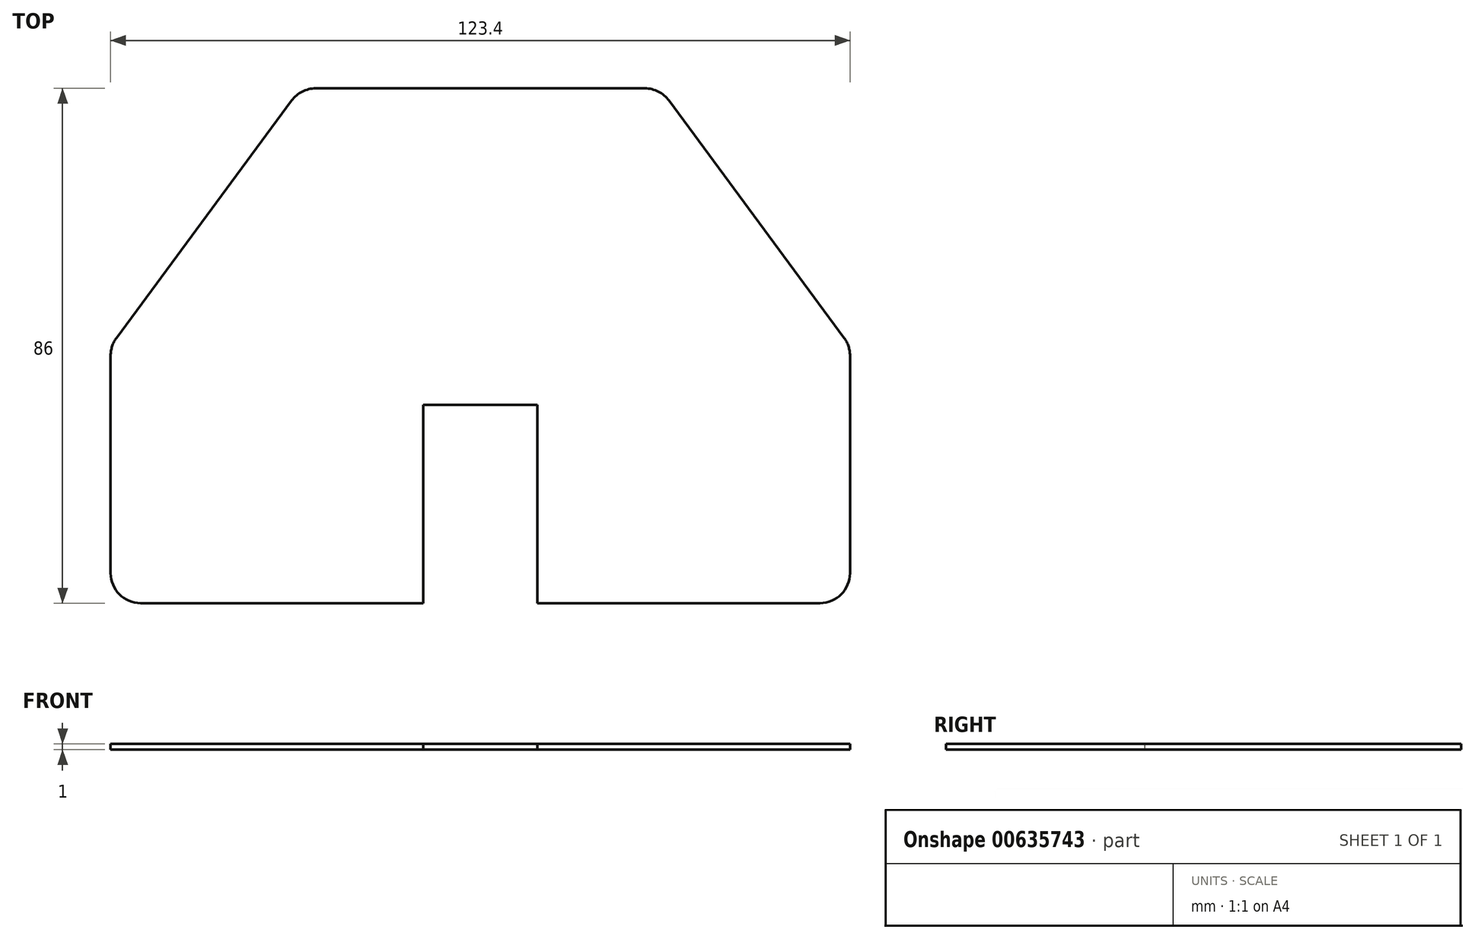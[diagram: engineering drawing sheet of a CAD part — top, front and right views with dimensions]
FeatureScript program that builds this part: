
annotation { "Feature Type Name" : "Feature", "Feature Type Description" : "" }
export const myFeature = defineFeature(function(context is Context, id is Id, definition is map)
    precondition{}
    {
        {
            var Q0;
            Q0=qCreatedBy(makeId("Top.planeOp"),FACE);
            var sketch = newSketch(context, id + "F0", { "sketchPlane" : qUnion([Q0])});
            skLineSegment(sketch, "E0.bottom", {"start": v(-61.7, 21.5) * mm, "end": v(61.7, 21.5) * mm});
            skLineSegment(sketch, "E0.top", {"start": v(-61.7, -21.5) * mm, "end": v(61.7, -21.5) * mm});
            skLineSegment(sketch, "E0.left", {"start": v(-61.7, 21.5) * mm, "end": v(-61.7, -21.5) * mm});
            skLineSegment(sketch, "E0.right", {"start": v(61.7, 21.5) * mm, "end": v(61.7, -21.5) * mm});
            skPoint(sketch, "E0.middle", {"position": v(0, 0) * mm});
            skLineSegment(sketch, "E1", {"start": v(0, 21.5) * mm, "end": v(0, 64.5) * mm});
            skPoint(sketch, "E1.endSnap0", {"position": v(0, 21.5) * mm});
            skLineSegment(sketch, "E2", {"start": v(0, 64.5) * mm, "end": v(30, 64.5) * mm});
            skLineSegment(sketch, "E3", {"start": v(0, 64.5) * mm, "end": v(-30, 64.5) * mm});
            skLineSegment(sketch, "E4", {"start": v(-30, 64.5) * mm, "end": v(-61.7, 21.5) * mm});
            skLineSegment(sketch, "E5", {"start": v(30, 64.5) * mm, "end": v(61.7, 21.5) * mm});
            skLineSegment(sketch, "E6.bottom", {"start": v(9.54, -21.5) * mm, "end": v(-9.54, -21.5) * mm});
            skLineSegment(sketch, "E6.top", {"start": v(9.54, 11.65) * mm, "end": v(-9.54, 11.65) * mm});
            skLineSegment(sketch, "E6.left", {"start": v(9.54, -21.5) * mm, "end": v(9.54, 11.65) * mm});
            skLineSegment(sketch, "E6.right", {"start": v(-9.54, -21.5) * mm, "end": v(-9.54, 11.65) * mm});
            skPoint(sketch, "E7", {"position": v(0, 11.65) * mm});
            skSolve(sketch);
        }
        {
            var Q0;
            {var subQ2=sQuery(id+"F0.wireOp",EDGE,"E1");Q0=makeQuery(id+"F0.imprint","IMPRINT",FACE,{"disambiguationData":[TD([[makeQuery(id+"F0.imprint","IMPRINT",EDGE,{"derivedFrom":subQ2}),1.0]])]});}
            var Q1;
            {var subQ2=sQuery(id+"F0.wireOp",EDGE,"E1");Q1=makeQuery(id+"F0.imprint","IMPRINT",FACE,{"disambiguationData":[TD([[makeQuery(id+"F0.imprint","IMPRINT",EDGE,{"derivedFrom":subQ2}),-1.0]])]});}
            var Q2;
            {var subQ5=sQuery(id+"F0.wireOp",EDGE,"E0.left");Q2=makeQuery(id+"F0.imprint","IMPRINT",FACE,{"disambiguationData":[TD([[makeQuery(id+"F0.imprint","IMPRINT",EDGE,{"derivedFrom":subQ5}),1.0]])]});}
            extrude(context, id + "F1", {"entities" : qUnion([Q0, Q1, Q2]), "depth" : 1 * mm, "offsetDistance" : 25 * mm});
        }
        {
            var Q0;
            Q0=makeQuery(id+"F1.opExtrude","SWEPT_EDGE",EDGE,{"disambiguationData":[OSD([sQuery(id+"F0.wireOp",EDGE,"E3"),sQuery(id+"F0.wireOp",EDGE,"E4")])]});
            var Q1;
            Q1=makeQuery(id+"F1.opExtrude","SWEPT_EDGE",EDGE,{"disambiguationData":[OSD([sQuery(id+"F0.wireOp",EDGE,"E0.bottom"),sQuery(id+"F0.wireOp",EDGE,"E0.left"),sQuery(id+"F0.wireOp",EDGE,"E4")])]});
            var Q2;
            Q2=makeQuery(id+"F1.opExtrude","SWEPT_EDGE",EDGE,{"disambiguationData":[OSD([sQuery(id+"F0.wireOp",EDGE,"E2"),sQuery(id+"F0.wireOp",EDGE,"E5")])]});
            var Q3;
            Q3=makeQuery(id+"F1.opExtrude","SWEPT_EDGE",EDGE,{"disambiguationData":[OSD([sQuery(id+"F0.wireOp",EDGE,"E0.bottom"),sQuery(id+"F0.wireOp",EDGE,"E0.right"),sQuery(id+"F0.wireOp",EDGE,"E5")])]});
            var Q4;
            Q4=makeQuery(id+"F1.opExtrude","SWEPT_EDGE",EDGE,{"disambiguationData":[OSD([sQuery(id+"F0.wireOp",EDGE,"E0.top"),sQuery(id+"F0.wireOp",EDGE,"E0.right")])]});
            var Q5;
            Q5=makeQuery(id+"F1.opExtrude","SWEPT_EDGE",EDGE,{"disambiguationData":[OSD([sQuery(id+"F0.wireOp",EDGE,"E0.top"),sQuery(id+"F0.wireOp",EDGE,"E0.left")])]});
            fillet(context, id + "F2", {"entities" : qUnion([Q0, Q1, Q2, Q3, Q4, Q5]), "radius" : 5 * mm, "tangentPropagation" : true, "allowEdgeOverflow" : false});
        }
    });
